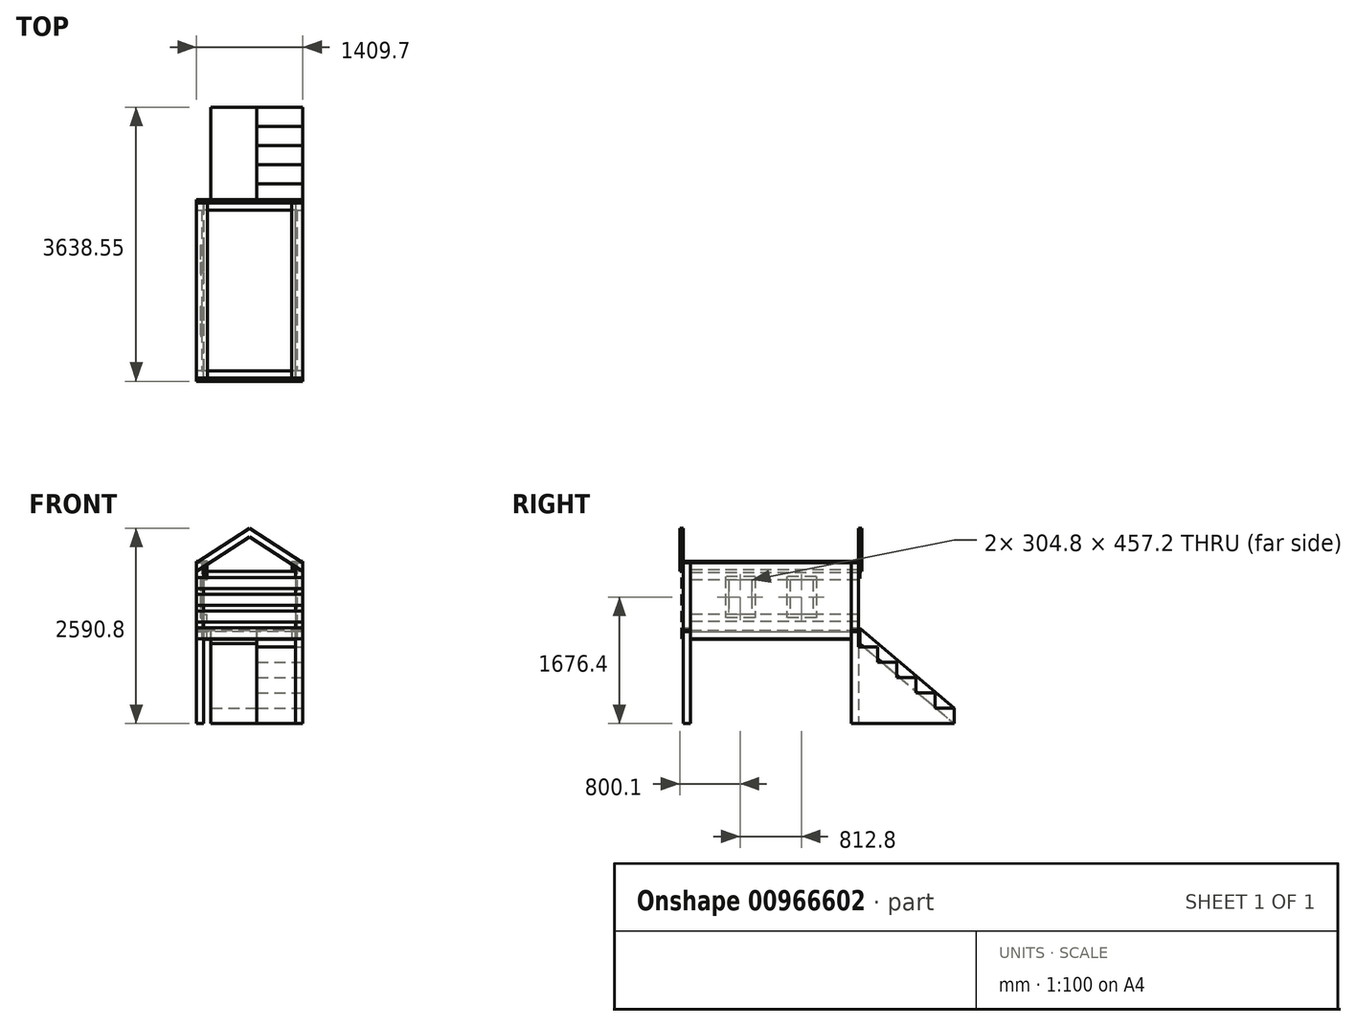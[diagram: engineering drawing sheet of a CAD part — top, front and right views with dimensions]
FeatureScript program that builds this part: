
annotation { "Feature Type Name" : "Feature", "Feature Type Description" : "" }
export const myFeature = defineFeature(function(context is Context, id is Id, definition is map)
    precondition{}
    {
        {
            var Q0;
            Q0=qCreatedBy(makeId("Top.planeOp"),FACE);
            var sketch = newSketch(context, id + "F0", { "sketchPlane" : qUnion([Q0])});
            skLineSegment(sketch, "E0.bottom", {"start": v(0, 0) * mm, "end": v(95.25, 0) * mm});
            skLineSegment(sketch, "E0.top", {"start": v(0, 95.25) * mm, "end": v(95.25, 95.25) * mm});
            skLineSegment(sketch, "E0.left", {"start": v(0, 0) * mm, "end": v(0, 95.25) * mm});
            skLineSegment(sketch, "E0.right", {"start": v(95.25, 0) * mm, "end": v(95.25, 95.25) * mm});
            skLineSegment(sketch, "E1.bottom", {"start": v(1314.45, 95.25) * mm, "end": v(1409.7, 95.25) * mm});
            skLineSegment(sketch, "E1.top", {"start": v(1314.45, 0) * mm, "end": v(1409.7, 0) * mm});
            skLineSegment(sketch, "E1.left", {"start": v(1314.45, 95.25) * mm, "end": v(1314.45, 0) * mm});
            skLineSegment(sketch, "E1.right", {"start": v(1409.7, 95.25) * mm, "end": v(1409.7, 0) * mm});
            skLineSegment(sketch, "E2.bottom", {"start": v(0, -2133.6) * mm, "end": v(95.25, -2133.6) * mm});
            skLineSegment(sketch, "E2.top", {"start": v(0, -2228.85) * mm, "end": v(95.25, -2228.85) * mm});
            skLineSegment(sketch, "E2.left", {"start": v(0, -2133.6) * mm, "end": v(0, -2228.85) * mm});
            skLineSegment(sketch, "E2.right", {"start": v(95.25, -2133.6) * mm, "end": v(95.25, -2228.85) * mm});
            skLineSegment(sketch, "E3.bottom", {"start": v(1314.45, -2133.6) * mm, "end": v(1409.7, -2133.6) * mm});
            skLineSegment(sketch, "E3.top", {"start": v(1314.45, -2228.85) * mm, "end": v(1409.7, -2228.85) * mm});
            skLineSegment(sketch, "E3.left", {"start": v(1314.45, -2133.6) * mm, "end": v(1314.45, -2228.85) * mm});
            skLineSegment(sketch, "E3.right", {"start": v(1409.7, -2133.6) * mm, "end": v(1409.7, -2228.85) * mm});
            skSolve(sketch);
        }
        {
            var Q0;
            Q0=makeQuery(id+"F0.imprint","IMPRINT",FACE,{"disambiguationData":[TD([[makeQuery(id+"F0.imprint","IMPRINT",EDGE,{"derivedFrom":sQuery(id+"F0.wireOp",EDGE,"E0.bottom")}),1.0]])]});
            var Q1;
            Q1=makeQuery(id+"F0.imprint","IMPRINT",FACE,{"disambiguationData":[TD([[makeQuery(id+"F0.imprint","IMPRINT",EDGE,{"derivedFrom":sQuery(id+"F0.wireOp",EDGE,"E1.bottom")}),-1.0]])]});
            var Q2;
            Q2=makeQuery(id+"F0.imprint","IMPRINT",FACE,{"disambiguationData":[TD([[makeQuery(id+"F0.imprint","IMPRINT",EDGE,{"derivedFrom":sQuery(id+"F0.wireOp",EDGE,"E3.bottom")}),-1.0]])]});
            var Q3;
            Q3=makeQuery(id+"F0.imprint","IMPRINT",FACE,{"disambiguationData":[TD([[makeQuery(id+"F0.imprint","IMPRINT",EDGE,{"derivedFrom":sQuery(id+"F0.wireOp",EDGE,"E2.bottom")}),-1.0]])]});
            extrude(context, id + "F1", {"entities" : qUnion([Q0, Q1, Q2, Q3]), "depth" : 2133.6 * mm, "offsetDistance" : 25.4 * mm});
        }
        {
            var Q0;
            Q0=qCreatedBy(makeId("Top.planeOp"),FACE);
            cPlane(context, id + "F2", {"entities" : qUnion([Q0]), "cplaneType" : CPlaneType.OFFSET, "offset" : 1219.2 * mm, "width" : 152.4 * mm, "height" : 152.4 * mm});
        }
        {
            var Q0;
            Q0=qCreatedBy(id+"F2.planeOp",FACE);
            var sketch = newSketch(context, id + "F3", { "sketchPlane" : qUnion([Q0])});
            skLineSegment(sketch, "E4.0.0", {"start": v(0, -2133.6) * mm, "end": v(0, -2228.85) * mm});
            skLineSegment(sketch, "E4.0.1", {"start": v(0, -2228.85) * mm, "end": v(95.25, -2228.85) * mm});
            skLineSegment(sketch, "E4.0.2", {"start": v(95.25, -2228.85) * mm, "end": v(95.25, -2133.6) * mm});
            skLineSegment(sketch, "E4.0.3", {"start": v(95.25, -2133.6) * mm, "end": v(0, -2133.6) * mm});
            skLineSegment(sketch, "E5.0.0", {"start": v(95.25, 95.25) * mm, "end": v(0, 95.25) * mm});
            skLineSegment(sketch, "E5.0.1", {"start": v(0, 95.25) * mm, "end": v(0, 0) * mm});
            skLineSegment(sketch, "E5.0.2", {"start": v(0, 0) * mm, "end": v(95.25, 0) * mm});
            skLineSegment(sketch, "E5.0.3", {"start": v(95.25, 0) * mm, "end": v(95.25, 95.25) * mm});
            skLineSegment(sketch, "E6.0.0", {"start": v(1314.45, 95.25) * mm, "end": v(1314.45, 0) * mm});
            skLineSegment(sketch, "E6.0.1", {"start": v(1314.45, 0) * mm, "end": v(1409.7, 0) * mm});
            skLineSegment(sketch, "E6.0.2", {"start": v(1409.7, 0) * mm, "end": v(1409.7, 95.25) * mm});
            skLineSegment(sketch, "E6.0.3", {"start": v(1409.7, 95.25) * mm, "end": v(1314.45, 95.25) * mm});
            skLineSegment(sketch, "E7.0.0", {"start": v(1314.45, -2133.6) * mm, "end": v(1314.45, -2228.85) * mm});
            skLineSegment(sketch, "E7.0.1", {"start": v(1314.45, -2228.85) * mm, "end": v(1409.7, -2228.85) * mm});
            skLineSegment(sketch, "E7.0.2", {"start": v(1409.7, -2228.85) * mm, "end": v(1409.7, -2133.6) * mm});
            skLineSegment(sketch, "E7.0.3", {"start": v(1409.7, -2133.6) * mm, "end": v(1314.45, -2133.6) * mm});
            skLineSegment(sketch, "E8.bottom", {"start": v(95.25, -2133.6) * mm, "end": v(1314.45, -2133.6) * mm});
            skLineSegment(sketch, "E8.top", {"start": v(95.25, 0) * mm, "end": v(1314.45, 0) * mm});
            skLineSegment(sketch, "E8.left", {"start": v(95.25, -2133.6) * mm, "end": v(95.25, 0) * mm});
            skLineSegment(sketch, "E8.right", {"start": v(1314.45, -2133.6) * mm, "end": v(1314.45, 0) * mm});
            skSolve(sketch);
        }
        {
            var Q0;
            Q0 = qSketchRegion(id + "F3", true);
            extrude(context, id + "F4", {"entities" : qUnion([Q0]), "depth" : 19.05 * mm, "offsetDistance" : 25.4 * mm});
        }
        {
            var Q0;
            Q0=qCreatedBy(id+"F2.planeOp",FACE);
            var sketch = newSketch(context, id + "F5", { "sketchPlane" : qUnion([Q0])});
            skPoint(sketch, "E9.0", {"position": v(95.25, -2228.85) * mm});
            skPoint(sketch, "E10.0", {"position": v(95.25, 95.25) * mm});
            skPoint(sketch, "E11.0", {"position": v(1314.45, 95.25) * mm});
            skPoint(sketch, "E12.0", {"position": v(1314.45, -2228.85) * mm});
            skLineSegment(sketch, "E13.bottom", {"start": v(95.25, -2228.85) * mm, "end": v(139.7, -2228.85) * mm});
            skLineSegment(sketch, "E13.top", {"start": v(95.25, 95.25) * mm, "end": v(139.7, 95.25) * mm});
            skLineSegment(sketch, "E13.left", {"start": v(95.25, -2228.85) * mm, "end": v(95.25, 95.25) * mm});
            skLineSegment(sketch, "E13.right", {"start": v(139.7, -2228.85) * mm, "end": v(139.7, 95.25) * mm});
            skLineSegment(sketch, "E14.bottom", {"start": v(1314.45, -2228.85) * mm, "end": v(1270, -2228.85) * mm});
            skLineSegment(sketch, "E14.top", {"start": v(1314.45, 95.25) * mm, "end": v(1270, 95.25) * mm});
            skLineSegment(sketch, "E14.left", {"start": v(1314.45, -2228.85) * mm, "end": v(1314.45, 95.25) * mm});
            skLineSegment(sketch, "E14.right", {"start": v(1270, -2228.85) * mm, "end": v(1270, 95.25) * mm});
            skSolve(sketch);
        }
        {
            var Q0;
            Q0 = qSketchRegion(id + "F5", true);
            extrude(context, id + "F6", {"entities" : qUnion([Q0]), "oppositeDirection" : true, "depth" : 95.25 * mm, "offsetDistance" : 25.4 * mm});
        }
        {
            var Q0;
            Q0=qCreatedBy(id+"F2.planeOp",FACE);
            cPlane(context, id + "F7", {"entities" : qUnion([Q0]), "cplaneType" : CPlaneType.OFFSET, "offset" : 228.6 * mm, "width" : 152.4 * mm, "height" : 152.4 * mm});
        }
        {
            var Q0;
            Q0=qCreatedBy(id+"F7.planeOp",FACE);
            var sketch = newSketch(context, id + "F8", { "sketchPlane" : qUnion([Q0])});
            skPoint(sketch, "E15.0", {"position": v(95.25, 95.25) * mm});
            skPoint(sketch, "E16.0", {"position": v(95.25, -2228.85) * mm});
            skLineSegment(sketch, "E17.bottom", {"start": v(95.25, 95.25) * mm, "end": v(139.7, 95.25) * mm});
            skLineSegment(sketch, "E17.top", {"start": v(95.25, -2228.85) * mm, "end": v(139.7, -2228.85) * mm});
            skLineSegment(sketch, "E17.left", {"start": v(95.25, 95.25) * mm, "end": v(95.25, -2228.85) * mm});
            skLineSegment(sketch, "E17.right", {"start": v(139.7, 95.25) * mm, "end": v(139.7, -2228.85) * mm});
            skSolve(sketch);
        }
        {
            var Q0;
            Q0 = qSketchRegion(id + "F8", true);
            extrude(context, id + "F9", {"entities" : qUnion([Q0]), "oppositeDirection" : true, "depth" : 95.25 * mm, "offsetDistance" : 25.4 * mm});
        }
        {
            var Q0;
            Q0=qCreatedBy(id+"F7.planeOp",FACE);
            cPlane(context, id + "F10", {"entities" : qUnion([Q0]), "cplaneType" : CPlaneType.OFFSET, "offset" : 457.2 * mm, "width" : 152.4 * mm, "height" : 152.4 * mm});
        }
        {
            var Q0;
            Q0=qCreatedBy(id+"F10.planeOp",FACE);
            var sketch = newSketch(context, id + "F11", { "sketchPlane" : qUnion([Q0])});
            skLineSegment(sketch, "E18.0", {"start": v(139.7, 95.25) * mm, "end": v(139.7, -2228.85) * mm});
            skLineSegment(sketch, "E19.0", {"start": v(95.25, 95.25) * mm, "end": v(95.25, -2228.85) * mm});
            skLineSegment(sketch, "E20.bottom", {"start": v(139.7, 95.25) * mm, "end": v(95.25, 95.25) * mm});
            skLineSegment(sketch, "E20.top", {"start": v(139.7, -2228.85) * mm, "end": v(95.25, -2228.85) * mm});
            skSolve(sketch);
        }
        {
            var Q0;
            Q0 = qSketchRegion(id + "F11", true);
            extrude(context, id + "F12", {"entities" : qUnion([Q0]), "depth" : 95.25 * mm, "offsetDistance" : 25.4 * mm});
        }
        {
            var Q0;
            Q0=makeQuery(id+"F12.opExtrude","SWEPT_FACE",FACE,{"disambiguationData":[OSD([sQuery(id+"F11.wireOp",EDGE,"E19.0")])]});
            var sketch = newSketch(context, id + "F13", { "sketchPlane" : qUnion([Q0])});
            skLineSegment(sketch, "E21.bottom", {"start": v(0, 2133.6) * mm, "end": v(2133.6, 2133.6) * mm});
            skLineSegment(sketch, "E21.top", {"start": v(0, 1117.6) * mm, "end": v(2133.6, 1117.6) * mm});
            skLineSegment(sketch, "E21.left", {"start": v(0, 2133.6) * mm, "end": v(0, 1117.6) * mm});
            skLineSegment(sketch, "E21.right", {"start": v(2133.6, 2133.6) * mm, "end": v(2133.6, 1117.6) * mm});
            skLineSegment(sketch, "E22.bottom", {"start": v(508, 1905) * mm, "end": v(812.8, 1905) * mm});
            skLineSegment(sketch, "E22.top", {"start": v(508, 1447.8) * mm, "end": v(812.8, 1447.8) * mm});
            skLineSegment(sketch, "E22.left", {"start": v(508, 1905) * mm, "end": v(508, 1447.8) * mm});
            skLineSegment(sketch, "E22.right", {"start": v(812.8, 1905) * mm, "end": v(812.8, 1447.8) * mm});
            skLineSegment(sketch, "E23.bottom", {"start": v(1320.8, 1905) * mm, "end": v(1625.6, 1905) * mm});
            skLineSegment(sketch, "E23.top", {"start": v(1320.8, 1447.8) * mm, "end": v(1625.6, 1447.8) * mm});
            skLineSegment(sketch, "E23.left", {"start": v(1320.8, 1905) * mm, "end": v(1320.8, 1447.8) * mm});
            skLineSegment(sketch, "E23.right", {"start": v(1625.6, 1905) * mm, "end": v(1625.6, 1447.8) * mm});
            skSolve(sketch);
        }
        {
            var Q0;
            {var subQ0=sQuery(id+"F13.wireOp",EDGE,"E21.bottom");Q0=makeQuery(id+"F13.imprint","IMPRINT",FACE,{"disambiguationData":[TD([[makeQuery(id+"F13.imprint","IMPRINT",EDGE,{"derivedFrom":subQ0}),-1.0]])]});}
            var Q1;
            {var subQ7=sQuery(id+"F13.wireOp",EDGE,"E22.bottom");Q1=makeQuery(id+"F13.imprint","IMPRINT",FACE,{"disambiguationData":[TD([[makeQuery(id+"F13.imprint","IMPRINT",EDGE,{"derivedFrom":subQ7}),1.0]])]});}
            var Q2;
            {var subQ3=sQuery(id+"F13.wireOp",EDGE,"E21.top");Q2=makeQuery(id+"F13.imprint","IMPRINT",FACE,{"disambiguationData":[TD([[makeQuery(id+"F13.imprint","IMPRINT",EDGE,{"derivedFrom":subQ3}),1.0]])]});}
            extrude(context, id + "F14", {"entities" : qUnion([Q0, Q1, Q2]), "depth" : 25.4 * mm, "offsetDistance" : 25.4 * mm});
        }
        {
            var Q0;
            Q0=qCreatedBy(id+"F2.planeOp",FACE);
            var sketch = newSketch(context, id + "F15", { "sketchPlane" : qUnion([Q0])});
            skLineSegment(sketch, "E24.bottom", {"start": v(1314.45, 95.25) * mm, "end": v(95.25, 95.25) * mm});
            skLineSegment(sketch, "E24.top", {"start": v(1314.45, 0) * mm, "end": v(95.25, 0) * mm});
            skLineSegment(sketch, "E24.left", {"start": v(1314.45, 95.25) * mm, "end": v(1314.45, 0) * mm});
            skLineSegment(sketch, "E24.right", {"start": v(95.25, 95.25) * mm, "end": v(95.25, 0) * mm});
            skLineSegment(sketch, "E25.bottom", {"start": v(1314.45, -2133.6) * mm, "end": v(95.25, -2133.6) * mm});
            skLineSegment(sketch, "E25.top", {"start": v(1314.45, -2228.85) * mm, "end": v(95.25, -2228.85) * mm});
            skLineSegment(sketch, "E25.left", {"start": v(1314.45, -2133.6) * mm, "end": v(1314.45, -2228.85) * mm});
            skLineSegment(sketch, "E25.right", {"start": v(95.25, -2133.6) * mm, "end": v(95.25, -2228.85) * mm});
            skSolve(sketch);
        }
        {
            var Q0;
            Q0 = qSketchRegion(id + "F15", true);
            extrude(context, id + "F16", {"entities" : qUnion([Q0]), "depth" : 44.45 * mm, "offsetDistance" : 25.4 * mm});
        }
        {
            var Q0;
            Q0=makeQuery(id+"F1.opExtrude","CAP_FACE",FACE,{"disambiguationData":[OSD([sQuery(id+"F0.wireOp",EDGE,"E2.bottom"),sQuery(id+"F0.wireOp",EDGE,"E2.top"),sQuery(id+"F0.wireOp",EDGE,"E2.left"),sQuery(id+"F0.wireOp",EDGE,"E2.right")])],"isStart":false});
            var sketch = newSketch(context, id + "F17", { "sketchPlane" : qUnion([Q0])});
            skLineSegment(sketch, "E26.bottom", {"start": v(95.25, 95.25) * mm, "end": v(139.7, 95.25) * mm});
            skLineSegment(sketch, "E26.top", {"start": v(95.25, -2228.85) * mm, "end": v(139.7, -2228.85) * mm});
            skLineSegment(sketch, "E26.left", {"start": v(95.25, 95.25) * mm, "end": v(95.25, -2228.85) * mm});
            skLineSegment(sketch, "E26.right", {"start": v(139.7, 95.25) * mm, "end": v(139.7, -2228.85) * mm});
            skLineSegment(sketch, "E27.bottom", {"start": v(1270, 95.25) * mm, "end": v(1314.45, 95.25) * mm});
            skLineSegment(sketch, "E27.top", {"start": v(1270, -2228.85) * mm, "end": v(1314.45, -2228.85) * mm});
            skLineSegment(sketch, "E27.left", {"start": v(1270, 95.25) * mm, "end": v(1270, -2228.85) * mm});
            skLineSegment(sketch, "E27.right", {"start": v(1314.45, 95.25) * mm, "end": v(1314.45, -2228.85) * mm});
            skSolve(sketch);
        }
        {
            var Q0;
            Q0 = qSketchRegion(id + "F17", true);
            extrude(context, id + "F18", {"entities" : qUnion([Q0]), "oppositeDirection" : true, "depth" : 95.25 * mm, "offsetDistance" : 25.4 * mm});
        }
        {
            var Q0;
            Q0=makeQuery(id+"F1.opExtrude","SWEPT_FACE",FACE,{"disambiguationData":[OSD([sQuery(id+"F0.wireOp",EDGE,"E2.top")])]});
            var sketch = newSketch(context, id + "F19", { "sketchPlane" : qUnion([Q0])});
            skLineSegment(sketch, "E28", {"start": v(0, 2133.6) * mm, "end": v(704.85, 2590.8) * mm});
            skLineSegment(sketch, "E29", {"start": v(704.85, 2590.8) * mm, "end": v(704.85, 2477.27) * mm});
            skLineSegment(sketch, "E30", {"start": v(704.85, 2590.8) * mm, "end": v(1409.7, 2133.6) * mm});
            skLineSegment(sketch, "E31", {"start": v(1409.7, 2020.07) * mm, "end": v(704.85, 2477.27) * mm});
            skLineSegment(sketch, "E32", {"start": v(0, 2020.07) * mm, "end": v(704.85, 2477.27) * mm});
            skLineSegment(sketch, "E33", {"start": v(0, 2133.6) * mm, "end": v(0, 2020.07) * mm});
            skLineSegment(sketch, "E34", {"start": v(1409.7, 2133.6) * mm, "end": v(1409.7, 2020.07) * mm});
            skSolve(sketch);
        }
        {
            var Q0;
            Q0 = qSketchRegion(id + "F19", true);
            extrude(context, id + "F20", {"entities" : qUnion([Q0]), "depth" : 44.45 * mm, "offsetDistance" : 25.4 * mm});
        }
        {
            var Q0;
            Q0=makeQuery(id+"F1.opExtrude","SWEPT_FACE",FACE,{"disambiguationData":[OSD([sQuery(id+"F0.wireOp",EDGE,"E1.bottom")])]});
            var sketch = newSketch(context, id + "F21", { "sketchPlane" : qUnion([Q0])});
            skLineSegment(sketch, "E35.0.0", {"start": v(-704.85, 2590.8) * mm, "end": v(-1409.7, 2133.6) * mm});
            skLineSegment(sketch, "E35.0.1", {"start": v(-1409.7, 2133.6) * mm, "end": v(-1409.7, 2020.07) * mm});
            skLineSegment(sketch, "E35.0.2", {"start": v(-1409.7, 2020.07) * mm, "end": v(-704.85, 2477.27) * mm});
            skLineSegment(sketch, "E35.0.3", {"start": v(-704.85, 2477.27) * mm, "end": v(0, 2020.07) * mm});
            skLineSegment(sketch, "E35.0.4", {"start": v(0, 2020.07) * mm, "end": v(0, 2133.6) * mm});
            skLineSegment(sketch, "E35.0.5", {"start": v(0, 2133.6) * mm, "end": v(-704.85, 2590.8) * mm});
            skSolve(sketch);
        }
        {
            var Q0;
            Q0 = qSketchRegion(id + "F21", true);
            extrude(context, id + "F22", {"entities" : qUnion([Q0]), "depth" : 44.45 * mm, "offsetDistance" : 25.4 * mm});
        }
        {
            var Q0;
            Q0=makeQuery(id+"F1.opExtrude","SWEPT_FACE",FACE,{"disambiguationData":[OSD([sQuery(id+"F0.wireOp",EDGE,"E2.top")])]});
            var sketch = newSketch(context, id + "F23", { "sketchPlane" : qUnion([Q0])});
            skLineSegment(sketch, "E36.bottom", {"start": v(0, 1123.95) * mm, "end": v(1409.7, 1123.95) * mm});
            skLineSegment(sketch, "E36.top", {"start": v(0, 1270) * mm, "end": v(1409.7, 1270) * mm});
            skLineSegment(sketch, "E36.left", {"start": v(0, 1123.95) * mm, "end": v(0, 1270) * mm});
            skLineSegment(sketch, "E36.right", {"start": v(1409.7, 1123.95) * mm, "end": v(1409.7, 1270) * mm});
            skLineSegment(sketch, "E37.bottom", {"start": v(0, 1492.25) * mm, "end": v(1409.7, 1492.25) * mm});
            skLineSegment(sketch, "E37.top", {"start": v(0, 1346.2) * mm, "end": v(1409.7, 1346.2) * mm});
            skLineSegment(sketch, "E37.left", {"start": v(0, 1492.25) * mm, "end": v(0, 1346.2) * mm});
            skLineSegment(sketch, "E37.right", {"start": v(1409.7, 1492.25) * mm, "end": v(1409.7, 1346.2) * mm});
            skLineSegment(sketch, "E38.bottom", {"start": v(0, 1714.5) * mm, "end": v(1409.7, 1714.5) * mm});
            skLineSegment(sketch, "E38.top", {"start": v(0, 1568.45) * mm, "end": v(1409.7, 1568.45) * mm});
            skLineSegment(sketch, "E38.left", {"start": v(0, 1714.5) * mm, "end": v(0, 1568.45) * mm});
            skLineSegment(sketch, "E38.right", {"start": v(1409.7, 1714.5) * mm, "end": v(1409.7, 1568.45) * mm});
            skLineSegment(sketch, "E39.bottom", {"start": v(0, 1790.7) * mm, "end": v(1409.7, 1790.7) * mm});
            skLineSegment(sketch, "E39.left", {"start": v(0, 1790.7) * mm, "end": v(0, 1716.7) * mm});
            skLineSegment(sketch, "E39.right", {"start": v(1409.7, 1790.7) * mm, "end": v(1409.7, 1716.7) * mm});
            skLineSegment(sketch, "E40.bottom", {"start": v(0, 1936.75) * mm, "end": v(1409.7, 1936.75) * mm});
            skLineSegment(sketch, "E40.left", {"start": v(0, 1936.75) * mm, "end": v(0, 1790.7) * mm});
            skLineSegment(sketch, "E40.right", {"start": v(1409.7, 1936.75) * mm, "end": v(1409.7, 1790.7) * mm});
            skSolve(sketch);
        }
        {
            var Q0;
            Q0 = qSketchRegion(id + "F23", true);
            extrude(context, id + "F24", {"entities" : qUnion([Q0]), "depth" : 19.05 * mm, "offsetDistance" : 25.4 * mm});
        }
        {
            var Q0;
            Q0=makeQuery(id+"F18.opExtrude","SWEPT_FACE",FACE,{"disambiguationData":[OSD([sQuery(id+"F17.wireOp",EDGE,"E27.right")])]});
            var sketch = newSketch(context, id + "F25", { "sketchPlane" : qUnion([Q0])});
            skLineSegment(sketch, "E41.bottom", {"start": v(-2133.6, 2133.6) * mm, "end": v(0, 2133.6) * mm});
            skLineSegment(sketch, "E41.top", {"start": v(-2133.6, 1123.95) * mm, "end": v(0, 1123.95) * mm});
            skLineSegment(sketch, "E41.left", {"start": v(-2133.6, 2133.6) * mm, "end": v(-2133.6, 1123.95) * mm});
            skLineSegment(sketch, "E41.right", {"start": v(0, 2133.6) * mm, "end": v(0, 1123.95) * mm});
            skSolve(sketch);
        }
        {
            var Q0;
            Q0 = qSketchRegion(id + "F25", true);
            extrude(context, id + "F26", {"entities" : qUnion([Q0]), "depth" : 19.05 * mm, "offsetDistance" : 25.4 * mm});
        }
        {
            var Q0;
            Q0=makeQuery(id+"F1.opExtrude","SWEPT_FACE",FACE,{"disambiguationData":[OSD([sQuery(id+"F0.wireOp",EDGE,"E0.top")])]});
            var sketch = newSketch(context, id + "F27", { "sketchPlane" : qUnion([Q0])});
            skLineSegment(sketch, "E42.bottom", {"start": v(-1409.7, 1263.65) * mm, "end": v(0, 1263.65) * mm});
            skLineSegment(sketch, "E42.top", {"start": v(-1409.7, 1117.6) * mm, "end": v(0, 1117.6) * mm});
            skLineSegment(sketch, "E42.left", {"start": v(-1409.7, 1263.65) * mm, "end": v(-1409.7, 1117.6) * mm});
            skLineSegment(sketch, "E42.right", {"start": v(0, 1263.65) * mm, "end": v(0, 1117.6) * mm});
            skLineSegment(sketch, "E43.bottom", {"start": v(-1409.7, 2020.07) * mm, "end": v(0, 2020.07) * mm});
            skLineSegment(sketch, "E43.top", {"start": v(-1409.7, 1924.82) * mm, "end": v(0, 1924.82) * mm});
            skLineSegment(sketch, "E43.left", {"start": v(-1409.7, 2020.07) * mm, "end": v(-1409.7, 1924.82) * mm});
            skLineSegment(sketch, "E43.right", {"start": v(0, 2020.07) * mm, "end": v(0, 1924.82) * mm});
            skSolve(sketch);
        }
        {
            var Q0;
            {var subQ0=sQuery(id+"F27.wireOp",EDGE,"E43.left");Q0=makeQuery(id+"F27.imprint","IMPRINT",FACE,{"disambiguationData":[TD([[makeQuery(id+"F27.imprint","IMPRINT",EDGE,{"derivedFrom":subQ0}),1.0]])]});}
            var Q1;
            {var subQ0=sQuery(id+"F27.wireOp",EDGE,"E42.left");Q1=makeQuery(id+"F27.imprint","IMPRINT",FACE,{"disambiguationData":[TD([[makeQuery(id+"F27.imprint","IMPRINT",EDGE,{"derivedFrom":subQ0}),1.0]])]});}
            extrude(context, id + "F28", {"entities" : qUnion([Q0, Q1]), "depth" : 19.05 * mm, "offsetDistance" : 25.4 * mm});
        }
        {
            var Q0;
            Q0=makeQuery(id+"F1.opExtrude","CAP_FACE",FACE,{"disambiguationData":[OSD([sQuery(id+"F0.wireOp",EDGE,"E0.bottom"),sQuery(id+"F0.wireOp",EDGE,"E0.top"),sQuery(id+"F0.wireOp",EDGE,"E0.left"),sQuery(id+"F0.wireOp",EDGE,"E0.right")])],"isStart":false});
            var sketch = newSketch(context, id + "F29", { "sketchPlane" : qUnion([Q0])});
            skLineSegment(sketch, "E44.bottom", {"start": v(1263.65, 95.25) * mm, "end": v(1409.7, 95.25) * mm});
            skLineSegment(sketch, "E44.top", {"start": v(1263.65, -2228.85) * mm, "end": v(1409.7, -2228.85) * mm});
            skLineSegment(sketch, "E44.left", {"start": v(1263.65, 95.25) * mm, "end": v(1263.65, -2228.85) * mm});
            skLineSegment(sketch, "E44.right", {"start": v(1409.7, 95.25) * mm, "end": v(1409.7, -2228.85) * mm});
            skLineSegment(sketch, "E45.bottom", {"start": v(146.05, 95.25) * mm, "end": v(0, 95.25) * mm});
            skLineSegment(sketch, "E45.top", {"start": v(146.05, -2228.85) * mm, "end": v(0, -2228.85) * mm});
            skLineSegment(sketch, "E45.left", {"start": v(146.05, 95.25) * mm, "end": v(146.05, -2228.85) * mm});
            skLineSegment(sketch, "E45.right", {"start": v(0, 95.25) * mm, "end": v(0, -2228.85) * mm});
            skSolve(sketch);
        }
        {
            var Q0;
            Q0 = qSketchRegion(id + "F29", true);
            extrude(context, id + "F30", {"entities" : qUnion([Q0]), "depth" : 19.05 * mm, "offsetDistance" : 25.4 * mm});
        }
        {
            var Q0;
            Q0=makeQuery(id+"F1.opExtrude","SWEPT_FACE",FACE,{"disambiguationData":[OSD([sQuery(id+"F0.wireOp",EDGE,"E1.right")])]});
            var sketch = newSketch(context, id + "F31", { "sketchPlane" : qUnion([Q0])});
            skLineSegment(sketch, "E46", {"start": v(95.25, 1016) * mm, "end": v(349.25, 1016) * mm});
            skLineSegment(sketch, "E47", {"start": v(349.25, 1016) * mm, "end": v(349.25, 812.8) * mm});
            skLineSegment(sketch, "E48", {"start": v(349.25, 812.8) * mm, "end": v(603.25, 812.8) * mm});
            skLineSegment(sketch, "E49", {"start": v(603.25, 812.8) * mm, "end": v(603.25, 609.6) * mm});
            skLineSegment(sketch, "E50", {"start": v(603.25, 609.6) * mm, "end": v(857.25, 609.6) * mm});
            skLineSegment(sketch, "E51", {"start": v(857.25, 609.6) * mm, "end": v(857.25, 406.4) * mm});
            skLineSegment(sketch, "E52", {"start": v(857.25, 406.4) * mm, "end": v(1111.25, 406.4) * mm});
            skLineSegment(sketch, "E53", {"start": v(1111.25, 406.4) * mm, "end": v(1111.25, 203.2) * mm});
            skLineSegment(sketch, "E54", {"start": v(1111.25, 203.2) * mm, "end": v(1365.25, 203.2) * mm});
            skLineSegment(sketch, "E55", {"start": v(1365.25, 203.2) * mm, "end": v(1365.25, 0) * mm});
            skLineSegment(sketch, "E56", {"start": v(1365.25, 0) * mm, "end": v(95.25, 0) * mm});
            skLineSegment(sketch, "E57", {"start": v(95.25, 0) * mm, "end": v(95.25, 1016) * mm});
            skSolve(sketch);
        }
        {
            var Q0;
            Q0 = qSketchRegion(id + "F31", true);
            extrude(context, id + "F32", {"entities" : qUnion([Q0]), "operationType" : NewBodyOperationType.ADD, "oppositeDirection" : true, "depth" : 609.6 * mm, "offsetDistance" : 25.4 * mm});
        }
        {
            var Q0;
            Q0=makeQuery(id+"F32.opExtrude","CAP_FACE",FACE,{"disambiguationData":[OSD([sQuery(id+"F31.wireOp",EDGE,"E46"),sQuery(id+"F31.wireOp",EDGE,"E47"),sQuery(id+"F31.wireOp",EDGE,"E48"),sQuery(id+"F31.wireOp",EDGE,"E49"),sQuery(id+"F31.wireOp",EDGE,"E50"),sQuery(id+"F31.wireOp",EDGE,"E51"),sQuery(id+"F31.wireOp",EDGE,"E52"),sQuery(id+"F31.wireOp",EDGE,"E53"),sQuery(id+"F31.wireOp",EDGE,"E54"),sQuery(id+"F31.wireOp",EDGE,"E55"),sQuery(id+"F31.wireOp",EDGE,"E56"),sQuery(id+"F31.wireOp",EDGE,"E57")])],"isStart":false});
            var sketch = newSketch(context, id + "F33", { "sketchPlane" : qUnion([Q0])});
            skLineSegment(sketch, "E58", {"start": v(-1365.25, 203.2) * mm, "end": v(-114.3, 1263.65) * mm});
            skLineSegment(sketch, "E59", {"start": v(-114.3, 1263.65) * mm, "end": v(-114.3, 1060.45) * mm});
            skLineSegment(sketch, "E60", {"start": v(-114.3, 1060.45) * mm, "end": v(-1365.25, 0) * mm});
            skLineSegment(sketch, "E61", {"start": v(-1365.25, 0) * mm, "end": v(-1365.25, 203.2) * mm});
            skSolve(sketch);
        }
        {
            var Q0;
            Q0 = qSketchRegion(id + "F33", true);
            extrude(context, id + "F34", {"entities" : qUnion([Q0]), "depth" : 609.6 * mm, "offsetDistance" : 25.4 * mm});
        }
        {
            var Q0;
            Q0=makeQuery(id+"F14.opExtrude","CAP_FACE",FACE,{"disambiguationData":[OSD([sQuery(id+"F13.wireOp",EDGE,"E21.bottom"),sQuery(id+"F13.wireOp",EDGE,"E21.top"),sQuery(id+"F13.wireOp",EDGE,"E21.left"),sQuery(id+"F13.wireOp",EDGE,"E21.right"),sQuery(id+"F13.wireOp",EDGE,"E22.bottom"),sQuery(id+"F13.wireOp",EDGE,"E22.top"),sQuery(id+"F13.wireOp",EDGE,"E22.left"),sQuery(id+"F13.wireOp",EDGE,"E22.right"),sQuery(id+"F13.wireOp",EDGE,"E23.bottom"),sQuery(id+"F13.wireOp",EDGE,"E23.top"),sQuery(id+"F13.wireOp",EDGE,"E23.left"),sQuery(id+"F13.wireOp",EDGE,"E23.right")])],"isStart":false});
            var sketch = newSketch(context, id + "F35", { "sketchPlane" : qUnion([Q0])});
            skLineSegment(sketch, "E62.bottom", {"start": v(463.55, 1949.45) * mm, "end": v(857.25, 1949.45) * mm});
            skLineSegment(sketch, "E62.top", {"start": v(463.55, 1403.35) * mm, "end": v(857.25, 1403.35) * mm});
            skLineSegment(sketch, "E62.left", {"start": v(463.55, 1949.45) * mm, "end": v(463.55, 1403.35) * mm});
            skLineSegment(sketch, "E62.right", {"start": v(857.25, 1949.45) * mm, "end": v(857.25, 1403.35) * mm});
            skLineSegment(sketch, "E63.bottom", {"start": v(1276.35, 1949.45) * mm, "end": v(1670.05, 1949.45) * mm});
            skLineSegment(sketch, "E63.top", {"start": v(1276.35, 1403.35) * mm, "end": v(1670.05, 1403.35) * mm});
            skLineSegment(sketch, "E63.left", {"start": v(1276.35, 1949.45) * mm, "end": v(1276.35, 1403.35) * mm});
            skLineSegment(sketch, "E63.right", {"start": v(1670.05, 1949.45) * mm, "end": v(1670.05, 1403.35) * mm});
            skLineSegment(sketch, "E64.bottom", {"start": v(508, 1905) * mm, "end": v(812.8, 1905) * mm});
            skLineSegment(sketch, "E64.top", {"start": v(508, 1447.8) * mm, "end": v(812.8, 1447.8) * mm});
            skLineSegment(sketch, "E64.left", {"start": v(508, 1905) * mm, "end": v(508, 1447.8) * mm});
            skLineSegment(sketch, "E64.right", {"start": v(812.8, 1905) * mm, "end": v(812.8, 1447.8) * mm});
            skLineSegment(sketch, "E65.bottom", {"start": v(1320.8, 1905) * mm, "end": v(1625.6, 1905) * mm});
            skLineSegment(sketch, "E65.top", {"start": v(1320.8, 1447.8) * mm, "end": v(1625.6, 1447.8) * mm});
            skLineSegment(sketch, "E65.left", {"start": v(1320.8, 1905) * mm, "end": v(1320.8, 1447.8) * mm});
            skLineSegment(sketch, "E65.right", {"start": v(1625.6, 1905) * mm, "end": v(1625.6, 1447.8) * mm});
            skSolve(sketch);
        }
        {
            var Q0;
            Q0 = qSketchRegion(id + "F35", true);
            extrude(context, id + "F36", {"entities" : qUnion([Q0]), "operationType" : NewBodyOperationType.ADD, "depth" : 19.05 * mm, "offsetDistance" : 25.4 * mm});
        }
    });
